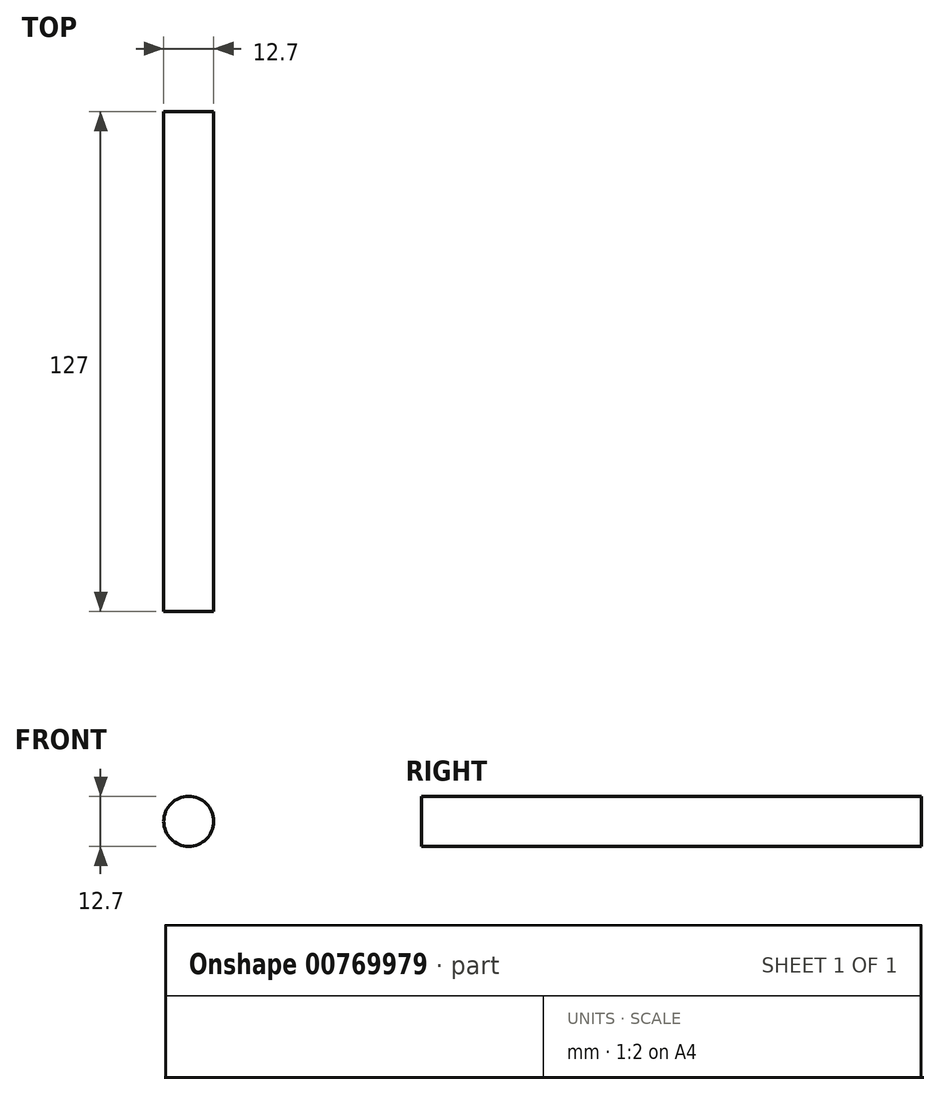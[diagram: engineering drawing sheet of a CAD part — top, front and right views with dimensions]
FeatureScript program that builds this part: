
annotation { "Feature Type Name" : "Feature", "Feature Type Description" : "" }
export const myFeature = defineFeature(function(context is Context, id is Id, definition is map)
    precondition{}
    {
        {
            var Q0;
            Q0=qCreatedBy(makeId("Front.planeOp"),FACE);
            var sketch = newSketch(context, id + "F0", { "sketchPlane" : qUnion([Q0])});
            skCircle(sketch, "E0", {"center": v(-22.38, 38.07) * mm, "radius": 6.35 * mm});
            skSolve(sketch);
        }
        {
            var Q0;
            Q0=makeQuery(id+"F0.imprint","IMPRINT",FACE,{"disambiguationData":[TD([[makeQuery(id+"F0.imprint","IMPRINT",EDGE,{"derivedFrom":sQuery(id+"F0.wireOp",EDGE,"E0")}),1.0]])]});
            extrude(context, id + "F1", {"entities" : qUnion([Q0]), "depth" : 127 * mm, "offsetDistance" : 25.4 * mm});
        }
    });
